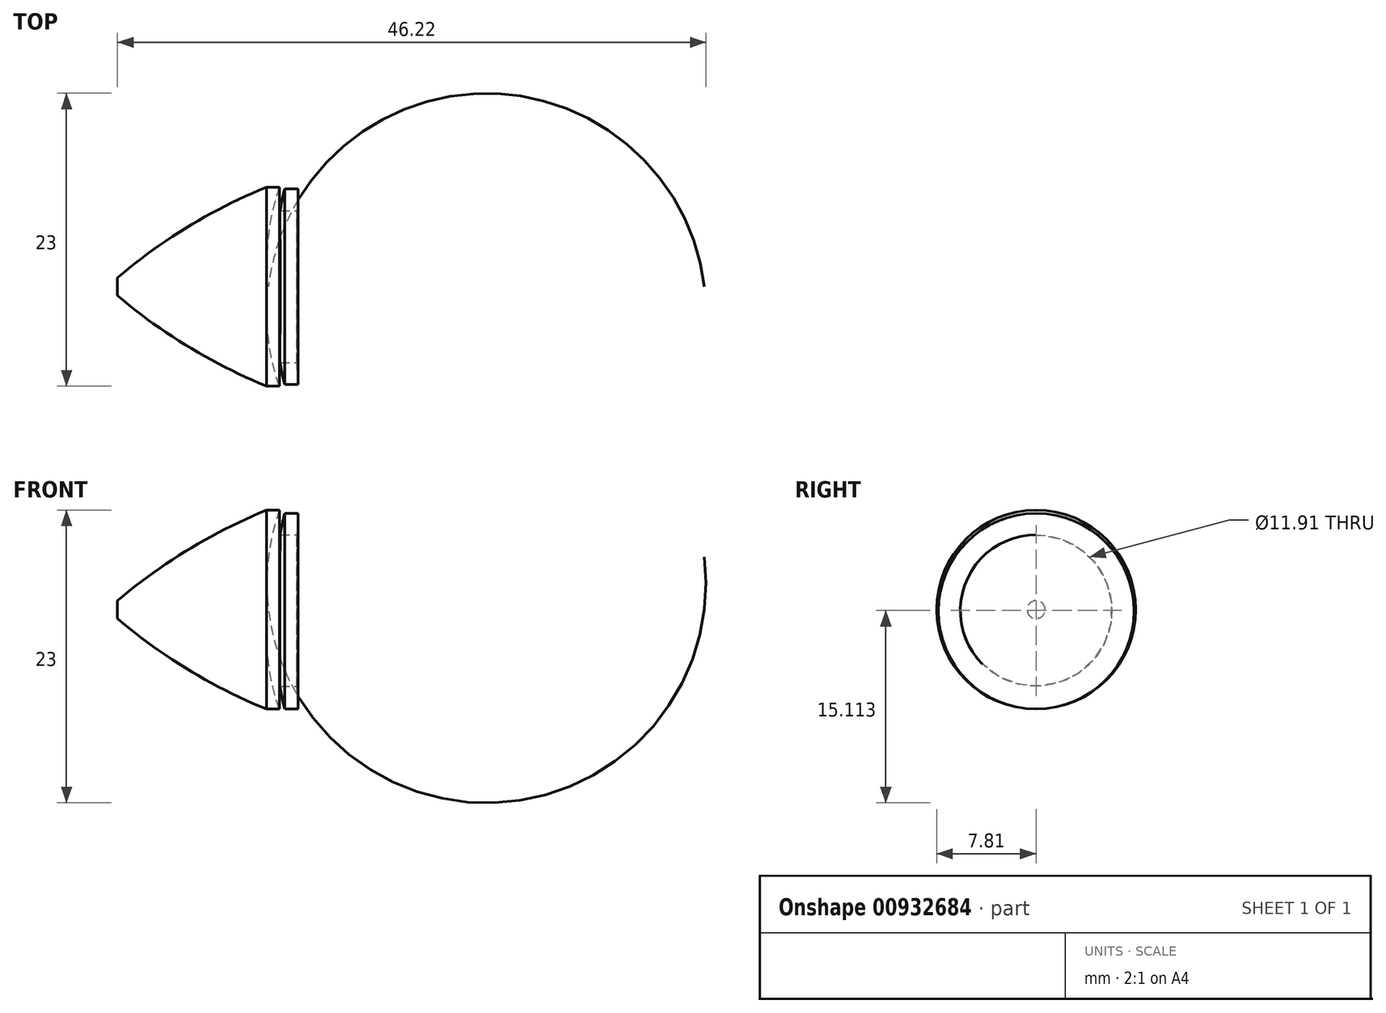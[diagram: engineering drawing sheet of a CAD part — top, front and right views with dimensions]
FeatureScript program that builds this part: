
annotation { "Feature Type Name" : "Feature", "Feature Type Description" : "" }
export const myFeature = defineFeature(function(context is Context, id is Id, definition is map)
    precondition{}
    {
        {
            var Q0;
            Q0=qCreatedBy(makeId("Front.planeOp"),FACE);
            var sketch = newSketch(context, id + "F0", { "sketchPlane" : qUnion([Q0])});
            skLineSegment(sketch, "E0", {"start": v(-66.87, 2.13) * mm, "end": v(-66.87, 0.55) * mm});
            skLineSegment(sketch, "E1", {"start": v(-66.87, 1.34) * mm, "end": v(-54.75, 1.34) * mm});
            skLineSegment(sketch, "E2", {"start": v(-54.75, 1.34) * mm, "end": v(-52.93, 1.34) * mm});
            skArc(sketch, "E3", {"start": v(-52.71, 9.02) * mm, "mid": v(-52.89, 5.18) * mm, "end": v(-52.93, 1.34) * mm});
            skLineSegment(sketch, "E4", {"start": v(-52.71, 9.02) * mm, "end": v(-53.78, 9.02) * mm});
            skArc(sketch, "E5", {"start": v(-53.78, 9.02) * mm, "mid": v(-54.46, 5.2) * mm, "end": v(-54.75, 1.34) * mm});
            skSolve(sketch);
        }
        {
            var Q0;
            Q0=makeQuery(id+"F0.imprint","IMPRINT",FACE,{"disambiguationData":[TD([[makeQuery(id+"F0.imprint","IMPRINT",EDGE,{"derivedFrom":sQuery(id+"F0.wireOp",EDGE,"E2")}),1.0]])]});
            var Q1;
            Q1=sQuery(id+"F0.wireOp",EDGE,"E2");
            revolve(context, id + "F1", {"surfaceOperationType" : NewSurfaceOperationType.NEW, "entities" : qUnion([Q0]), "axis" : qUnion([Q1]), "revolveType" : RevolveType.FULL});
        }
        {
            var Q0;
            Q0=qCreatedBy(makeId("Right.planeOp"),FACE);
            var sketch = newSketch(context, id + "F2", { "sketchPlane" : qUnion([Q0])});
            skCircle(sketch, "E6", {"center": v(0, 1.38) * mm, "radius": 6.01 * mm});
            skSolve(sketch);
        }
        {
            var Q0;
            Q0=sQuery(id+"F2.wireOp",VERTEX,"E6.center");
            var Q1;
            Q1=makeQuery(id+"F1.opRevolve","SWEPT_BODY",BODY,{"disambiguationData":[OSD([sQuery(id+"F0.wireOp",EDGE,"E2"),sQuery(id+"F0.wireOp",EDGE,"E3"),sQuery(id+"F0.wireOp",EDGE,"E4"),sQuery(id+"F0.wireOp",EDGE,"E5")])]});
            hole(context, id + "F3", {"style" : HoleStyle.SIMPLE, "endStyle" : HoleEndStyle.THROUGH, "standardTappedOrClearance" : lookupTablePath({ "fit" : "Normal (ASME)", "standard" : "ANSI", "size" : "7/16", "type" : "Clearance" }), "standardBlindInLast" : lookupTablePath({ "fit" : "Normal", "standard" : "ANSI", "engagement" : "75%", "pitch" : "14 tpi", "size" : "7/16", "type" : "Clearance & tapped" }), "holeDiameter" : 11.9 * mm, "majorDiameter" : 6.35 * mm, "isTappedThrough" : true, "tappedDepth" : 12.7 * mm, "tapClearance" : 3, "locations" : qUnion([Q0]), "scope" : qUnion([Q1])});
        }
        {
            var Q0;
            Q0=qCreatedBy(makeId("Front.planeOp"),FACE);
            var sketch = newSketch(context, id + "F4", { "sketchPlane" : qUnion([Q0])});
            skLineSegment(sketch, "E7", {"start": v(-66.9, 2.16) * mm, "end": v(-66.9, 0.75) * mm});
            skLineSegment(sketch, "E8", {"start": v(-66.9, 1.45) * mm, "end": v(-55.05, 1.45) * mm});
            skArc(sketch, "E9", {"start": v(-54.18, 9.27) * mm, "mid": v(-55.07, 5.4) * mm, "end": v(-55.05, 1.45) * mm});
            skLineSegment(sketch, "E10", {"start": v(-54.18, 9.27) * mm, "end": v(-55.2, 9.27) * mm});
            skArc(sketch, "E11", {"start": v(-55.2, 9.27) * mm, "mid": v(-61.33, 6.17) * mm, "end": v(-66.9, 2.16) * mm});
            skSolve(sketch);
        }
        {
            var Q0;
            Q0 = qSketchRegion(id + "F4", true);
            var Q1;
            Q1=sQuery(id+"F4.wireOp",EDGE,"E8");
            revolve(context, id + "F5", {"surfaceOperationType" : NewSurfaceOperationType.NEW, "entities" : qUnion([Q0]), "axis" : qUnion([Q1]), "revolveType" : RevolveType.FULL});
        }
    });
